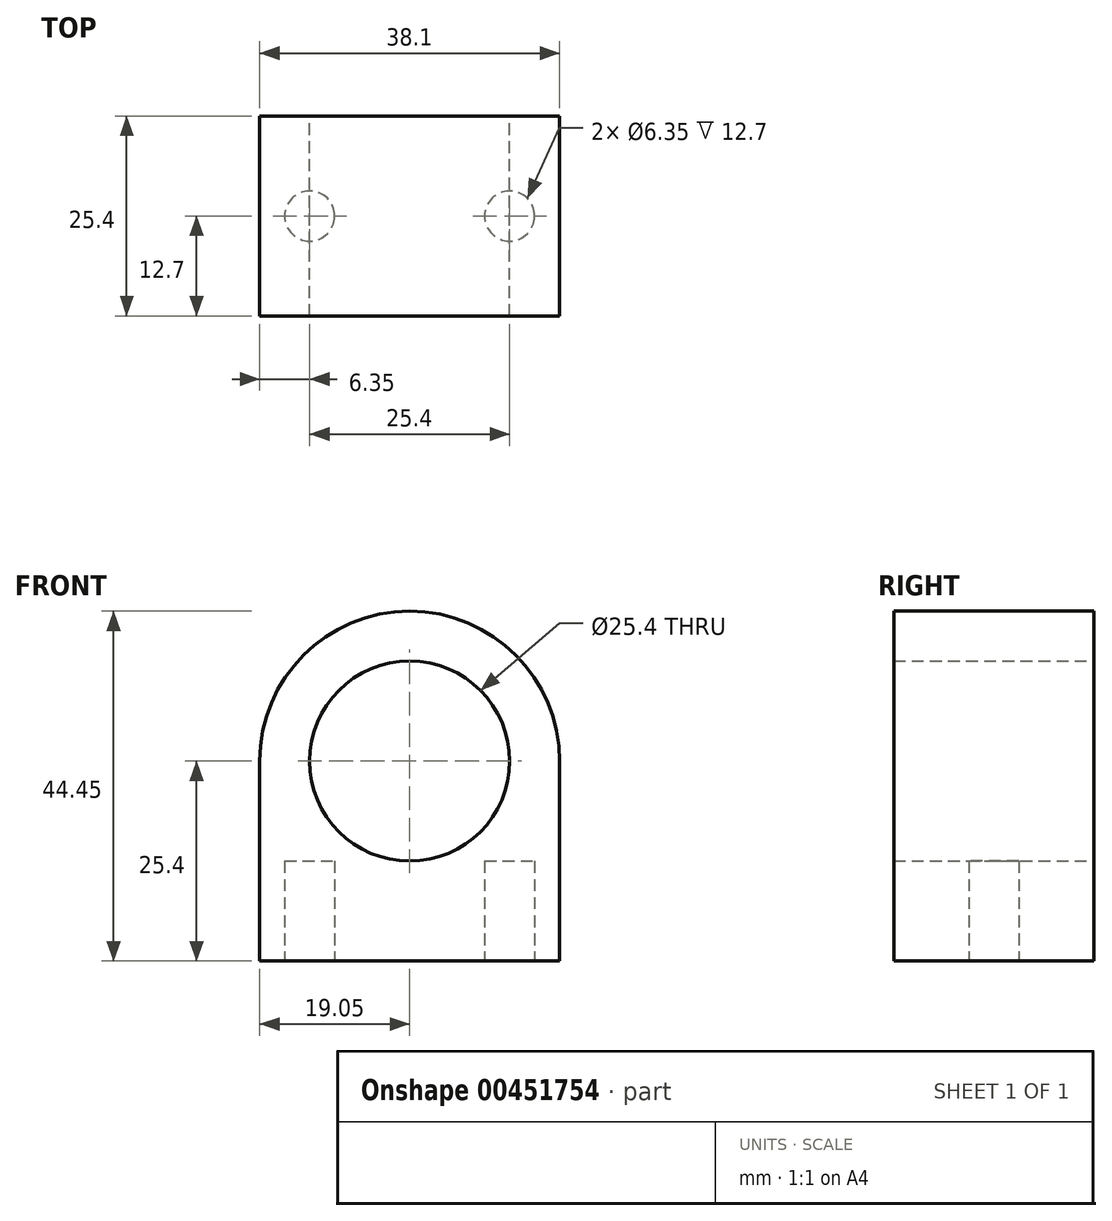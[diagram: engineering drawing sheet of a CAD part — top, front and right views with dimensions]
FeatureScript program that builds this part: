
annotation { "Feature Type Name" : "Feature", "Feature Type Description" : "" }
export const myFeature = defineFeature(function(context is Context, id is Id, definition is map)
    precondition{}
    {
        {
            var Q0;
            Q0=qCreatedBy(makeId("Front.planeOp"),FACE);
            var sketch = newSketch(context, id + "F0", { "sketchPlane" : qUnion([Q0])});
            skArc(sketch, "E0", {"start": v(19.05, 0) * mm, "mid": v(0, 19.05) * mm, "end": v(-19.05, 0) * mm});
            skLineSegment(sketch, "E1.top", {"start": v(-19.05, -25.4) * mm, "end": v(19.05, -25.4) * mm});
            skLineSegment(sketch, "E1.left", {"start": v(-19.05, 0) * mm, "end": v(-19.05, -25.4) * mm});
            skLineSegment(sketch, "E1.right", {"start": v(19.05, 0) * mm, "end": v(19.05, -25.4) * mm});
            skCircle(sketch, "E2", {"center": v(0, 0) * mm, "radius": 12.7 * mm});
            skSolve(sketch);
        }
        {
            var Q0;
            Q0 = qSketchRegion(id + "F0", true);
            extrude(context, id + "F1", {"entities" : qUnion([Q0]), "endBound" : BoundingType.SYMMETRIC, "depth" : 25.4 * mm});
        }
        {
            var Q0;
            Q0=makeQuery(id+"F1.opExtrude","SWEPT_FACE",FACE,{"disambiguationData":[OSD([sQuery(id+"F0.wireOp",EDGE,"E1.top")])]});
            var sketch = newSketch(context, id + "F2", { "sketchPlane" : qUnion([Q0])});
            skCircle(sketch, "E3", {"center": v(-12.7, 0) * mm, "radius": 3.18 * mm});
            skCircle(sketch, "E4", {"center": v(12.7, 0) * mm, "radius": 3.18 * mm});
            skSolve(sketch);
        }
        {
            var Q0;
            Q0 = qSketchRegion(id + "F2", true);
            extrude(context, id + "F3", {"entities" : qUnion([Q0]), "operationType" : NewBodyOperationType.REMOVE, "oppositeDirection" : true, "depth" : 12.7 * mm});
        }
    });
